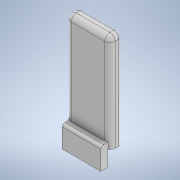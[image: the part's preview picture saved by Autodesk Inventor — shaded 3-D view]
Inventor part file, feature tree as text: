
AUTODESK INVENTOR PART (.ipt)
format: ipt  version: 2020 (Build 240168000, 168)  size: 153,088 bytes
history: native  units: mm
features: fillet x5, extrude x3, sketch x3
ambient origin geometry x8: Origin, YZ Plane, XZ Plane, XY Plane, X Axis, Y Axis, Z Axis, Center Point
bodies: Solid1 (feature_tree)
feature tree (11):
  extrude  "Extrusion1"  Depth=38.0mm
  fillet  "Fillet1"  Radius=4.0mm
  fillet  "Fillet2"  Radius=2.0mm
  extrude  "Extrusion2"  Depth=2.5mm
  fillet  "Fillet3"  Radius=6.0mm
  extrude  "Extrusion3"  Depth=2.5mm
  fillet  "Fillet4"  Radius=16.0mm
  fillet  "Fillet5"  Radius=0.5mm
  sketch  "Sketch1"  dims[d0=17.0mm d1=38.0mm d2=4.0mm d3=0.0mm d4=2.0mm]
  sketch  "Sketch2"  dims[d5=0.5mm d6=2.5mm d7=6.0mm]
  sketch  "Sketch3"  dims[d8=2.5mm d9=2.5mm d10=16.0mm d11=0.0mm d12=0.5mm d13=1.0mm d14=0.0mm d15=2.5mm d16=1.0mm]
